# Revit family: STC_A3-AU-Timber-Column-Stirrup-01
name_source: partatom
category: Structural Columns
revit_build: Autodesk Revit 2016 (Build: 20150220_1215(x64)
units: mm (PartAtom-declared; Revit-internal decimal feet)

## family parameters
Always export as geometry = No
Beam cutback in plan = From bounding box
Cut with Voids When Loaded = No
Material for Model Behavior = Other
Section Shape = Not Defined
Shared = No
Show family pre-cut in plan views = Yes

## types (3) — shared parameters
zero-valued in all types: A, Ix, Iy, Sx, Sy

## per-type parameters (varying)
| type | Material | Stirrup | b | d |
| 140 x 140 | <By Category> | <By Category> | 140 mm  [stored 0.459318 ft] | 140 mm  [stored 0.459318 ft] |
| 090x090 Column | Timber post | Steet galvanised | 90 mm  [stored 0.295276 ft] | 90 mm  [stored 0.295276 ft] |
| 100x100 | <By Category> | <By Category> | 100 mm  [stored 0.328084 ft] | 100 mm  [stored 0.328084 ft] |

note: [stored X ft] marks values corroborated as IEEE doubles in the binary element streams (Revit-internal decimal feet)

## geometry (parser evidence)
native form markers: Sweep x1
no freeform markers — native parametric forms only
